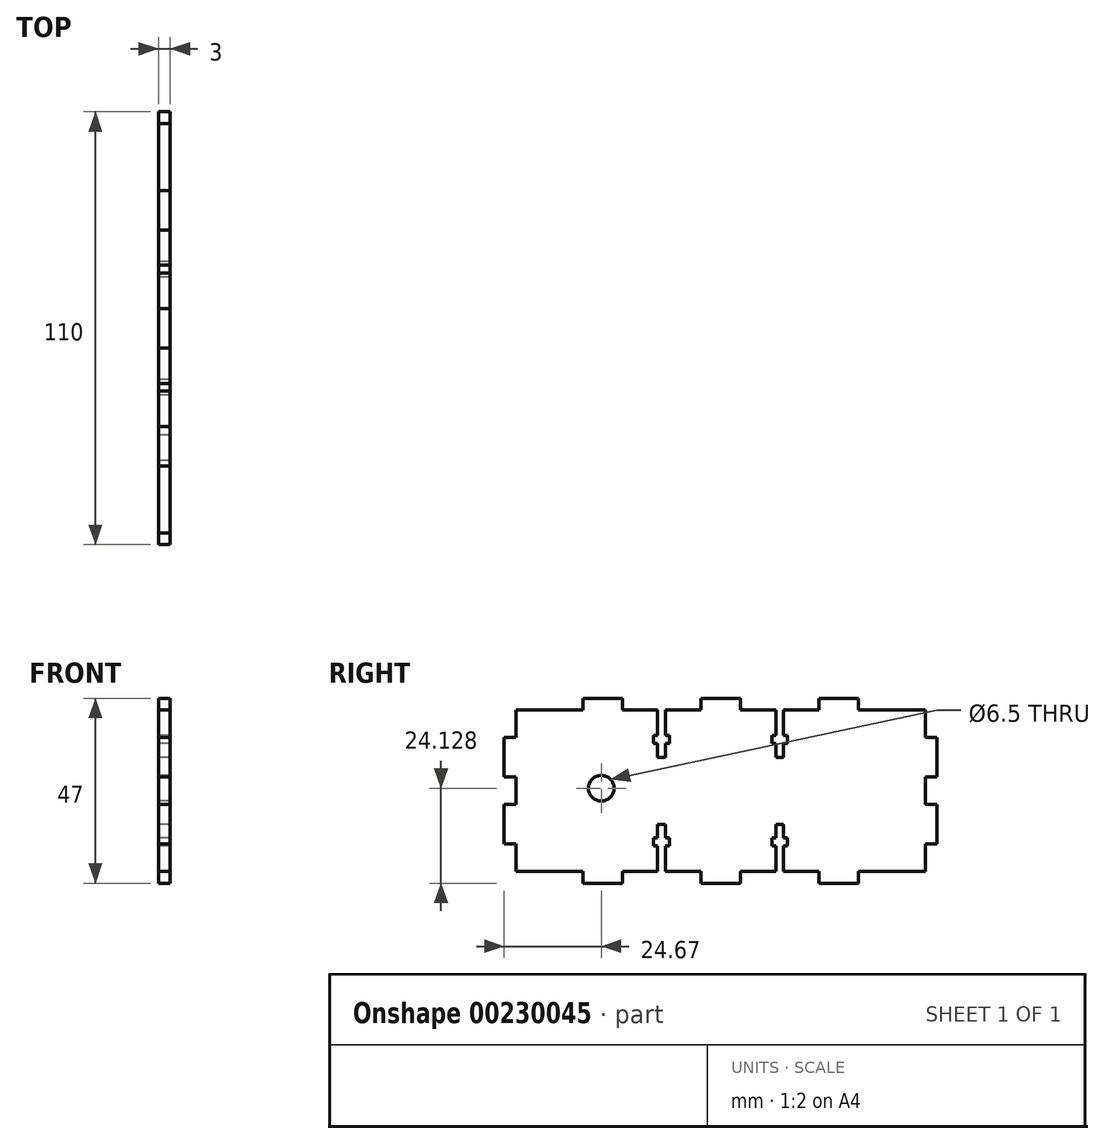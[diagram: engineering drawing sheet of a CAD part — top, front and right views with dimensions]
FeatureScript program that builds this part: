
annotation { "Feature Type Name" : "Feature", "Feature Type Description" : "" }
export const myFeature = defineFeature(function(context is Context, id is Id, definition is map)
    precondition{}
    {
        {
            var Q0;
            Q0=qCreatedBy(makeId("Right.planeOp"),FACE);
            var sketch = newSketch(context, id + "F0", { "sketchPlane" : qUnion([Q0])});
            skLineSegment(sketch, "E0", {"start": v(-38.37, -6.87) * mm, "end": v(-38.37, 0.13) * mm});
            skLineSegment(sketch, "E1", {"start": v(-38.37, 0.13) * mm, "end": v(-41.37, 0.13) * mm});
            skLineSegment(sketch, "E2", {"start": v(-41.37, 0.13) * mm, "end": v(-41.37, 10.13) * mm});
            skLineSegment(sketch, "E3", {"start": v(-41.37, 10.13) * mm, "end": v(-38.37, 10.13) * mm});
            skLineSegment(sketch, "E4", {"start": v(-38.37, 10.13) * mm, "end": v(-38.37, 17.13) * mm});
            skLineSegment(sketch, "E5", {"start": v(-38.37, 17.13) * mm, "end": v(-41.37, 17.13) * mm});
            skLineSegment(sketch, "E6", {"start": v(-41.37, 17.13) * mm, "end": v(-41.37, 27.13) * mm});
            skLineSegment(sketch, "E7", {"start": v(-41.37, 27.13) * mm, "end": v(-38.37, 27.13) * mm});
            skLineSegment(sketch, "E8", {"start": v(-38.37, 27.13) * mm, "end": v(-38.37, 34.13) * mm});
            skLineSegment(sketch, "E9", {"start": v(-38.37, 34.13) * mm, "end": v(-21.37, 34.13) * mm});
            skLineSegment(sketch, "E10", {"start": v(-21.37, 34.13) * mm, "end": v(-21.37, 37.13) * mm});
            skLineSegment(sketch, "E11", {"start": v(-21.37, 37.13) * mm, "end": v(-11.37, 37.13) * mm});
            skLineSegment(sketch, "E12", {"start": v(-11.37, 37.13) * mm, "end": v(-11.37, 34.13) * mm});
            skLineSegment(sketch, "E13", {"start": v(-11.37, 34.13) * mm, "end": v(-2.37, 34.13) * mm});
            skLineSegment(sketch, "E14", {"start": v(8.63, 34.13) * mm, "end": v(8.63, 37.13) * mm});
            skLineSegment(sketch, "E15", {"start": v(8.63, 37.13) * mm, "end": v(13.63, 37.13) * mm});
            skLineSegment(sketch, "E16", {"start": v(13.63, 37.13) * mm, "end": v(13.63, -6.87) * mm, "construction": true});
            skLineSegment(sketch, "E17.MirrorCS", {"start": v(8.63, -9.87) * mm, "end": v(13.63, -9.87) * mm});
            skLineSegment(sketch, "E18.MirrorCS", {"start": v(8.63, -6.87) * mm, "end": v(8.63, -9.87) * mm});
            skLineSegment(sketch, "E19.MirrorCS", {"start": v(-11.37, -9.87) * mm, "end": v(-11.37, -6.87) * mm});
            skLineSegment(sketch, "E20.MirrorCS", {"start": v(-41.37, 0.13) * mm, "end": v(-38.37, 0.13) * mm});
            skLineSegment(sketch, "E21.MirrorCS", {"start": v(-38.37, 10.13) * mm, "end": v(-41.37, 10.13) * mm});
            skLineSegment(sketch, "E22.MirrorCS", {"start": v(-21.37, -6.87) * mm, "end": v(-21.37, -9.87) * mm});
            skLineSegment(sketch, "E23.MirrorCS", {"start": v(-11.37, -6.87) * mm, "end": v(-2.37, -6.87) * mm});
            skLineSegment(sketch, "E24.MirrorCS", {"start": v(-21.37, -9.87) * mm, "end": v(-11.37, -9.87) * mm});
            skLineSegment(sketch, "E25.MirrorCS", {"start": v(-41.37, 10.13) * mm, "end": v(-41.37, 0.13) * mm});
            skLineSegment(sketch, "E26.MirrorCS", {"start": v(-38.37, 0.13) * mm, "end": v(-38.37, -6.87) * mm});
            skLineSegment(sketch, "E27.MirrorCS", {"start": v(-38.37, -6.87) * mm, "end": v(-21.37, -6.87) * mm});
            skLineSegment(sketch, "E28.MirrorCS", {"start": v(68.63, 0.13) * mm, "end": v(65.63, 0.13) * mm});
            skLineSegment(sketch, "E29.MirrorCS", {"start": v(68.63, 10.13) * mm, "end": v(65.63, 10.13) * mm});
            skLineSegment(sketch, "E30.MirrorCS", {"start": v(65.63, 10.13) * mm, "end": v(68.63, 10.13) * mm});
            skLineSegment(sketch, "E31.MirrorCS", {"start": v(65.63, 0.13) * mm, "end": v(68.63, 0.13) * mm});
            skLineSegment(sketch, "E32.MirrorCS", {"start": v(38.63, -9.87) * mm, "end": v(38.63, -6.87) * mm});
            skLineSegment(sketch, "E33.MirrorCS", {"start": v(48.63, -6.87) * mm, "end": v(48.63, -9.87) * mm});
            skLineSegment(sketch, "E34.MirrorCS", {"start": v(38.63, 37.13) * mm, "end": v(38.63, 34.13) * mm});
            skLineSegment(sketch, "E35.MirrorCS", {"start": v(48.63, 34.13) * mm, "end": v(48.63, 37.13) * mm});
            skLineSegment(sketch, "E36.MirrorCS", {"start": v(68.63, 27.13) * mm, "end": v(65.63, 27.13) * mm});
            skLineSegment(sketch, "E37.MirrorCS", {"start": v(65.63, 17.13) * mm, "end": v(68.63, 17.13) * mm});
            skLineSegment(sketch, "E38.MirrorCS", {"start": v(18.63, 34.13) * mm, "end": v(18.63, 37.13) * mm});
            skLineSegment(sketch, "E39.MirrorCS", {"start": v(18.63, -6.87) * mm, "end": v(18.63, -9.87) * mm});
            skLineSegment(sketch, "E40.MirrorCS", {"start": v(65.63, -6.87) * mm, "end": v(65.63, 0.13) * mm});
            skLineSegment(sketch, "E41.MirrorCS", {"start": v(65.63, 10.13) * mm, "end": v(65.63, 17.13) * mm});
            skLineSegment(sketch, "E42.MirrorCS", {"start": v(68.63, 10.13) * mm, "end": v(68.63, 0.13) * mm});
            skLineSegment(sketch, "E43.MirrorCS", {"start": v(18.63, -9.87) * mm, "end": v(13.63, -9.87) * mm});
            skLineSegment(sketch, "E44.MirrorCS", {"start": v(48.63, -9.87) * mm, "end": v(38.63, -9.87) * mm});
            skLineSegment(sketch, "E45.MirrorCS", {"start": v(65.63, 0.13) * mm, "end": v(65.63, -6.87) * mm});
            skLineSegment(sketch, "E46.MirrorCS", {"start": v(48.63, 37.13) * mm, "end": v(38.63, 37.13) * mm});
            skLineSegment(sketch, "E47.MirrorCS", {"start": v(65.63, 34.13) * mm, "end": v(48.63, 34.13) * mm});
            skLineSegment(sketch, "E48.MirrorCS", {"start": v(65.63, 27.13) * mm, "end": v(65.63, 34.13) * mm});
            skLineSegment(sketch, "E49.MirrorCS", {"start": v(68.63, 17.13) * mm, "end": v(68.63, 27.13) * mm});
            skLineSegment(sketch, "E50.MirrorCS", {"start": v(18.63, 37.13) * mm, "end": v(13.63, 37.13) * mm});
            skLineSegment(sketch, "E51.MirrorCS", {"start": v(38.63, 34.13) * mm, "end": v(29.63, 34.13) * mm});
            skLineSegment(sketch, "E52.MirrorCS", {"start": v(68.63, 0.13) * mm, "end": v(68.63, 10.13) * mm});
            skLineSegment(sketch, "E53.MirrorCS", {"start": v(38.63, -6.87) * mm, "end": v(29.63, -6.87) * mm});
            skLineSegment(sketch, "E54.MirrorCS", {"start": v(65.63, -6.87) * mm, "end": v(48.63, -6.87) * mm});
            skLineSegment(sketch, "E55.top", {"start": v(-2.37, 22.13) * mm, "end": v(-0.37, 22.13) * mm});
            skLineSegment(sketch, "E55.left", {"start": v(-2.37, 34.13) * mm, "end": v(-2.37, 27.63) * mm});
            skLineSegment(sketch, "E55.right", {"start": v(-0.37, 34.13) * mm, "end": v(-0.37, 27.63) * mm});
            skLineSegment(sketch, "E56.bottom", {"start": v(-3.37, 27.63) * mm, "end": v(-2.37, 27.63) * mm});
            skLineSegment(sketch, "E56.top", {"start": v(-3.37, 25.63) * mm, "end": v(-2.37, 25.63) * mm});
            skLineSegment(sketch, "E56.left", {"start": v(-3.37, 27.63) * mm, "end": v(-3.37, 25.63) * mm});
            skLineSegment(sketch, "E56.right", {"start": v(0.63, 27.63) * mm, "end": v(0.63, 25.63) * mm});
            skLineSegment(sketch, "E57.trimOffspring", {"start": v(-0.37, 34.13) * mm, "end": v(8.63, 34.13) * mm});
            skLineSegment(sketch, "E58.trimOffspring", {"start": v(-2.37, 25.63) * mm, "end": v(-2.37, 22.13) * mm});
            skLineSegment(sketch, "E59.trimOffspring", {"start": v(-0.37, 27.63) * mm, "end": v(0.63, 27.63) * mm});
            skLineSegment(sketch, "E60.trimOffspring", {"start": v(-0.37, 25.63) * mm, "end": v(-0.37, 22.13) * mm});
            skLineSegment(sketch, "E61.trimOffspring", {"start": v(-0.37, 25.63) * mm, "end": v(0.63, 25.63) * mm});
            skLineSegment(sketch, "E62.MirrorCS", {"start": v(-0.37, -0.37) * mm, "end": v(0.63, -0.37) * mm});
            skLineSegment(sketch, "E63.MirrorCS", {"start": v(-0.37, -6.87) * mm, "end": v(-0.37, -0.37) * mm});
            skLineSegment(sketch, "E64.MirrorCS", {"start": v(-3.37, -0.37) * mm, "end": v(-2.37, -0.37) * mm});
            skLineSegment(sketch, "E65.MirrorCS", {"start": v(-3.37, -0.37) * mm, "end": v(-3.37, 1.63) * mm});
            skLineSegment(sketch, "E66.MirrorCS", {"start": v(-3.37, 1.63) * mm, "end": v(-2.37, 1.63) * mm});
            skLineSegment(sketch, "E67.MirrorCS", {"start": v(-0.37, 1.63) * mm, "end": v(0.63, 1.63) * mm});
            skLineSegment(sketch, "E68.MirrorCS", {"start": v(-0.37, 1.63) * mm, "end": v(-0.37, 5.13) * mm});
            skLineSegment(sketch, "E69.MirrorCS", {"start": v(-2.37, 5.13) * mm, "end": v(-0.37, 5.13) * mm});
            skLineSegment(sketch, "E70.MirrorCS", {"start": v(-2.37, -6.87) * mm, "end": v(-2.37, -0.37) * mm});
            skLineSegment(sketch, "E71.MirrorCS", {"start": v(-2.37, 1.63) * mm, "end": v(-2.37, 5.13) * mm});
            skLineSegment(sketch, "E72.MirrorCS", {"start": v(0.63, -0.37) * mm, "end": v(0.63, 1.63) * mm});
            skLineSegment(sketch, "E73.MirrorCS", {"start": v(30.63, 27.63) * mm, "end": v(29.63, 27.63) * mm});
            skLineSegment(sketch, "E74.MirrorCS", {"start": v(29.63, 5.13) * mm, "end": v(27.63, 5.13) * mm});
            skLineSegment(sketch, "E75.MirrorCS", {"start": v(30.63, 27.63) * mm, "end": v(30.63, 25.63) * mm});
            skLineSegment(sketch, "E76.MirrorCS", {"start": v(27.63, -0.37) * mm, "end": v(26.63, -0.37) * mm});
            skLineSegment(sketch, "E77.MirrorCS", {"start": v(27.63, 1.63) * mm, "end": v(26.63, 1.63) * mm});
            skLineSegment(sketch, "E78.MirrorCS", {"start": v(30.63, 25.63) * mm, "end": v(29.63, 25.63) * mm});
            skLineSegment(sketch, "E79.MirrorCS", {"start": v(27.63, 25.63) * mm, "end": v(26.63, 25.63) * mm});
            skLineSegment(sketch, "E80.MirrorCS", {"start": v(30.63, -0.37) * mm, "end": v(29.63, -0.37) * mm});
            skLineSegment(sketch, "E81.MirrorCS", {"start": v(30.63, 1.63) * mm, "end": v(29.63, 1.63) * mm});
            skLineSegment(sketch, "E82.MirrorCS", {"start": v(29.63, 22.13) * mm, "end": v(27.63, 22.13) * mm});
            skLineSegment(sketch, "E83.MirrorCS", {"start": v(26.63, -0.37) * mm, "end": v(26.63, 1.63) * mm});
            skLineSegment(sketch, "E84.MirrorCS", {"start": v(26.63, 27.63) * mm, "end": v(26.63, 25.63) * mm});
            skLineSegment(sketch, "E85.MirrorCS", {"start": v(27.63, 27.63) * mm, "end": v(26.63, 27.63) * mm});
            skLineSegment(sketch, "E86.MirrorCS", {"start": v(30.63, -0.37) * mm, "end": v(30.63, 1.63) * mm});
            skLineSegment(sketch, "E87.MirrorCS", {"start": v(29.63, 34.13) * mm, "end": v(29.63, 27.63) * mm});
            skLineSegment(sketch, "E88.MirrorCS", {"start": v(29.63, 1.63) * mm, "end": v(29.63, 5.13) * mm});
            skLineSegment(sketch, "E89.MirrorCS", {"start": v(27.63, 1.63) * mm, "end": v(27.63, 5.13) * mm});
            skLineSegment(sketch, "E90.MirrorCS", {"start": v(27.63, 34.13) * mm, "end": v(27.63, 27.63) * mm});
            skLineSegment(sketch, "E91.MirrorCS", {"start": v(29.63, 25.63) * mm, "end": v(29.63, 22.13) * mm});
            skLineSegment(sketch, "E92.MirrorCS", {"start": v(27.63, 25.63) * mm, "end": v(27.63, 22.13) * mm});
            skLineSegment(sketch, "E93.MirrorCS", {"start": v(29.63, -6.87) * mm, "end": v(29.63, -0.37) * mm});
            skLineSegment(sketch, "E94.MirrorCS", {"start": v(27.63, -6.87) * mm, "end": v(27.63, -0.37) * mm});
            skLineSegment(sketch, "E95.trimOffspring", {"start": v(27.63, 34.13) * mm, "end": v(18.63, 34.13) * mm});
            skLineSegment(sketch, "E96.trimOffspring", {"start": v(27.63, -6.87) * mm, "end": v(18.63, -6.87) * mm});
            skLineSegment(sketch, "E97.trimOffspring", {"start": v(-0.37, -6.87) * mm, "end": v(8.63, -6.87) * mm});
            skPoint(sketch, "E98", {"position": v(43.63, 37.13) * mm});
            skPoint(sketch, "E99", {"position": v(65.63, 13.63) * mm});
            skCircle(sketch, "E100", {"center": v(-16.7, 14.26) * mm, "radius": 3.25 * mm});
            skSolve(sketch);
        }
        {
            var Q0;
            Q0=makeQuery(id+"F0.imprint","IMPRINT",FACE,{"disambiguationData":[TD([[makeQuery(id+"F0.imprint","IMPRINT",EDGE,{"derivedFrom":sQuery(id+"F0.wireOp",EDGE,"E4")}),-1.0]])]});
            extrude(context, id + "F1", {"entities" : qUnion([Q0]), "depth" : 3 * mm});
        }
    });
